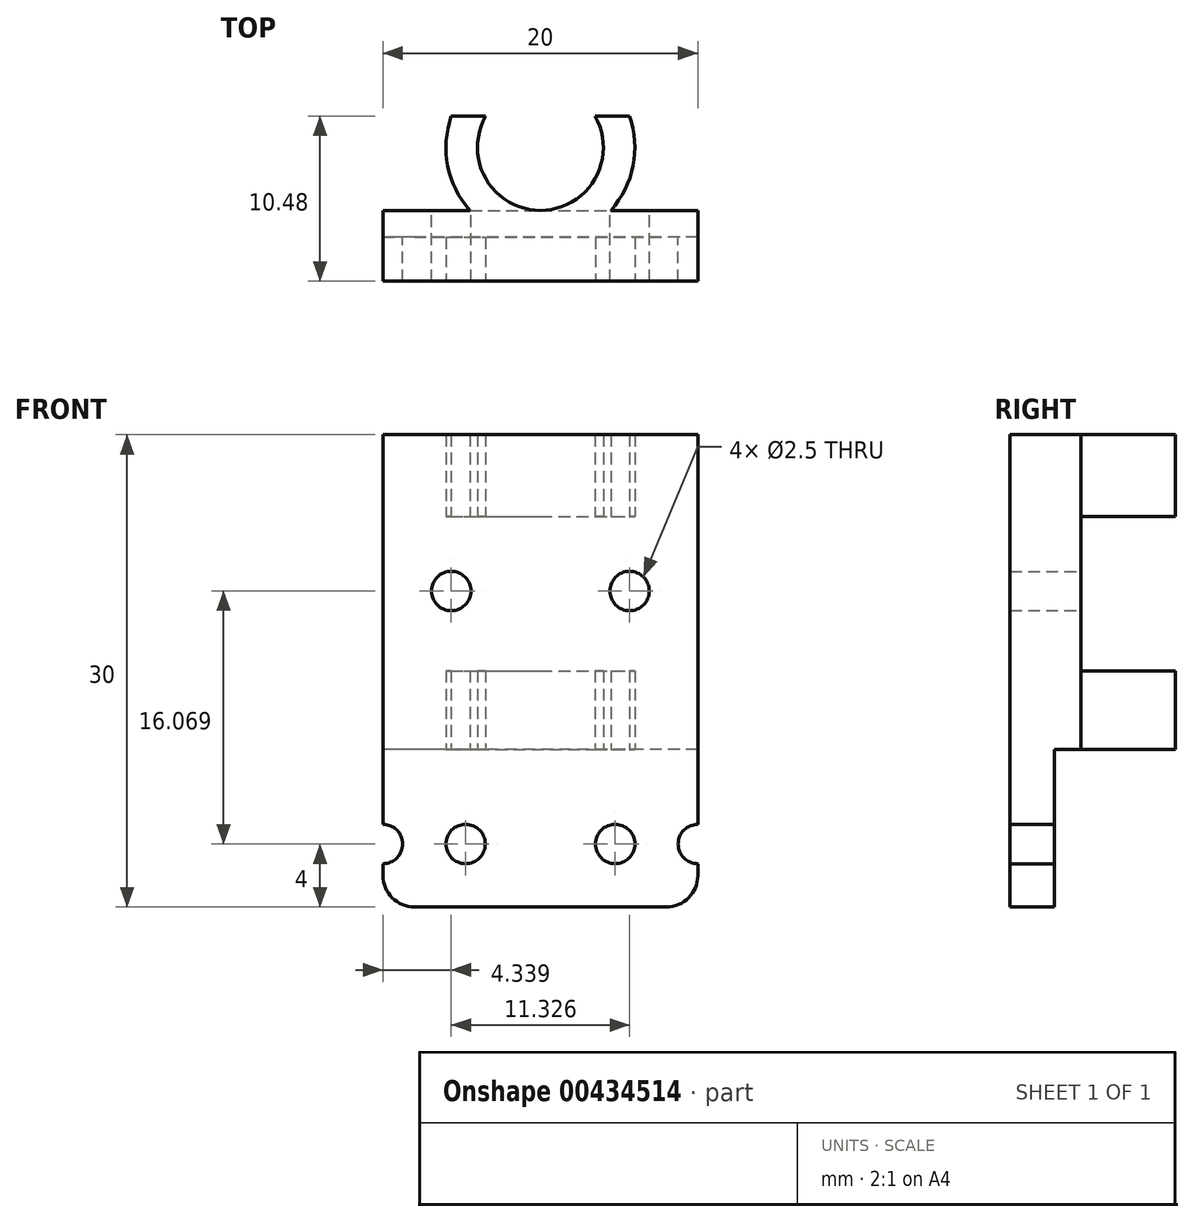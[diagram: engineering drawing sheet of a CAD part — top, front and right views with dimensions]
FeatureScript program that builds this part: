
annotation { "Feature Type Name" : "Feature", "Feature Type Description" : "" }
export const myFeature = defineFeature(function(context is Context, id is Id, definition is map)
    precondition{}
    {
        {
            var Q0;
            Q0=qCreatedBy(makeId("Top.planeOp"),FACE);
            var sketch = newSketch(context, id + "F0", { "sketchPlane" : qUnion([Q0])});
            skArc(sketch, "E0", {"start": v(-19.61, 7.8) * mm, "mid": v(-13.95, -0.17) * mm, "end": v(-8.28, 7.8) * mm});
            skLineSegment(sketch, "E1.right", {"start": v(278.54, 89.36) * mm, "end": v(278.54, 0) * mm});
            skArc(sketch, "E2", {"start": v(-17.42, 7.8) * mm, "mid": v(-13.95, 1.83) * mm, "end": v(-10.47, 7.8) * mm});
            skLineSegment(sketch, "E3.top", {"start": v(-19.61, 7.8) * mm, "end": v(-17.42, 7.8) * mm});
            skLineSegment(sketch, "E4.trimOffspring", {"start": v(-10.47, 7.8) * mm, "end": v(-8.28, 7.8) * mm});
            skPoint(sketch, "E5", {"position": v(-13.95, -1.45) * mm});
            skLineSegment(sketch, "E6", {"start": v(-13.95, 7.55) * mm, "end": v(-13.95, -10.44) * mm, "construction": true});
            skPoint(sketch, "E7.startSnap0", {"position": v(-13.95, 1.83) * mm});
            skSolve(sketch);
        }
        {
            var Q0;
            Q0=qSketchRegion(id+"F0",true);
            extrude(context, id + "F1", {"entities" : qUnion([Q0]), "depth" : 20 * mm});
        }
        {
            var Q0;
            Q0=qCreatedBy(makeId("Top.planeOp"),FACE);
            var sketch = newSketch(context, id + "F2", { "sketchPlane" : qUnion([Q0])});
            skArc(sketch, "E8.0.0", {"start": v(-17.42, 7.8) * mm, "mid": v(-13.95, 1.83) * mm, "end": v(-10.47, 7.8) * mm, "construction": true});
            skLineSegment(sketch, "E8.0.1", {"start": v(-10.47, 7.8) * mm, "end": v(-8.28, 7.8) * mm, "construction": true});
            skArc(sketch, "E8.0.2", {"start": v(-8.28, 7.8) * mm, "mid": v(-13.95, -0.17) * mm, "end": v(-19.61, 7.8) * mm, "construction": true});
            skLineSegment(sketch, "E8.0.3", {"start": v(-19.61, 7.8) * mm, "end": v(-17.42, 7.8) * mm, "construction": true});
            skPoint(sketch, "E9", {"position": v(-13.95, -0.17) * mm});
            skPoint(sketch, "E10", {"position": v(-13.95, 1.83) * mm});
            skLineSegment(sketch, "E11", {"start": v(-13.95, 1.83) * mm, "end": v(-3.95, 1.83) * mm});
            skLineSegment(sketch, "E12", {"start": v(-3.95, 1.83) * mm, "end": v(-3.95, -1.17) * mm});
            skLineSegment(sketch, "E13", {"start": v(-3.95, -1.17) * mm, "end": v(-23.95, -1.17) * mm});
            skLineSegment(sketch, "E14", {"start": v(-23.95, -1.17) * mm, "end": v(-23.95, 1.83) * mm});
            skLineSegment(sketch, "E15", {"start": v(-23.95, 1.83) * mm, "end": v(-13.95, 1.83) * mm});
            skSolve(sketch);
        }
        {
            var Q0;
            Q0=makeQuery(id+"F2.imprint","IMPRINT",FACE,{"disambiguationData":[TD([[makeQuery(id+"F2.imprint","IMPRINT",EDGE,{"derivedFrom":sQuery(id+"F2.wireOp",EDGE,"E11")}),-1.0]])]});
            extrude(context, id + "F3", {"entities" : qUnion([Q0]), "operationType" : NewBodyOperationType.ADD, "endBound" : BoundingType.SYMMETRIC, "depth" : 20 * mm});
        }
        {
            var Q0;
            Q0=qCreatedBy(makeId("Front.planeOp"),FACE);
            var sketch = newSketch(context, id + "F4", { "sketchPlane" : qUnion([Q0])});
            skCircle(sketch, "E16", {"center": v(-9.2, -6) * mm, "radius": 1.25 * mm});
            skPoint(sketch, "E17", {"position": v(-10.9, 30) * mm});
            skPoint(sketch, "E18.endSnap0", {"position": v(-14.04, 0) * mm});
            skLineSegment(sketch, "E19.0", {"start": v(-23.95, -10) * mm, "end": v(-3.95, -10) * mm, "construction": true});
            skPoint(sketch, "E20", {"position": v(-13.95, -10) * mm});
            skLineSegment(sketch, "E21", {"start": v(-13.95, -10) * mm, "end": v(-13.95, -0.98) * mm, "construction": true});
            skCircle(sketch, "E22.MirrorC", {"center": v(-18.7, -6) * mm, "radius": 1.25 * mm});
            skSolve(sketch);
        }
        {
            var Q0;
            Q0 = qSketchRegion(id + "F4", true);
            extrude(context, id + "F5", {"entities" : qUnion([Q0]), "operationType" : NewBodyOperationType.REMOVE, "endBound" : BoundingType.SYMMETRIC, "oppositeDirection" : true, "depth" : 4.4 * mm});
        }
        {
            var Q0;
            Q0=makeQuery(id+"F3.opExtrude","CAP_FACE",FACE,{"disambiguationData":[OSD([sQuery(id+"F2.wireOp",EDGE,"E11"),sQuery(id+"F2.wireOp",EDGE,"E12"),sQuery(id+"F2.wireOp",EDGE,"E13"),sQuery(id+"F2.wireOp",EDGE,"E14"),sQuery(id+"F2.wireOp",EDGE,"E15")])],"isStart":false});
            var sketch = newSketch(context, id + "F6", { "sketchPlane" : qUnion([Q0])});
            skArc(sketch, "E23.0.0", {"start": v(-9.48, 1.83) * mm, "mid": v(-13.95, -0.17) * mm, "end": v(-18.42, 1.83) * mm});
            skLineSegment(sketch, "E23.0.1", {"start": v(-18.42, 1.83) * mm, "end": v(-23.95, 1.83) * mm});
            skLineSegment(sketch, "E23.0.2", {"start": v(-23.95, 1.83) * mm, "end": v(-23.95, -1.17) * mm});
            skLineSegment(sketch, "E23.0.3", {"start": v(-23.95, -1.17) * mm, "end": v(-3.95, -1.17) * mm});
            skLineSegment(sketch, "E23.0.4", {"start": v(-3.95, -1.17) * mm, "end": v(-3.95, 1.83) * mm});
            skLineSegment(sketch, "E23.0.5", {"start": v(-3.95, 1.83) * mm, "end": v(-9.48, 1.83) * mm});
            skSolve(sketch);
        }
        {
            var Q0;
            Q0 = qSketchRegion(id + "F6", true);
            var Q1;
            Q1=makeQuery(id+"F1.opExtrude","CAP_FACE",FACE,{"disambiguationData":[OSD([sQuery(id+"F0.wireOp",EDGE,"E0"),sQuery(id+"F0.wireOp",EDGE,"E2"),sQuery(id+"F0.wireOp",EDGE,"E3.top"),sQuery(id+"F0.wireOp",EDGE,"E4.trimOffspring")])],"isStart":false});
            extrude(context, id + "F7", {"entities" : qUnion([Q0]), "operationType" : NewBodyOperationType.ADD, "endBound" : BoundingType.UP_TO_SURFACE, "endBoundEntityFace" : qUnion([Q1]), "depth" : 6.4 * mm});
        }
        {
            var Q0;
            Q0=makeQuery(id+"F7.boolean.opBoolean","MERGE",FACE,{"derivedFrom":[makeQuery(id+"F3.opExtrude","SWEPT_FACE",FACE,{"disambiguationData":[OSD([sQuery(id+"F2.wireOp",EDGE,"E11"),sQuery(id+"F2.wireOp",EDGE,"E15")])]}),makeQuery(id+"F7.opExtrude","SWEPT_FACE",FACE,{"disambiguationData":[OSD([sQuery(id+"F6.wireOp",EDGE,"E23.0.1")])]}),makeQuery(id+"F7.opExtrude","SWEPT_FACE",FACE,{"disambiguationData":[OSD([sQuery(id+"F6.wireOp",EDGE,"E23.0.5")])]})]});
            cPlane(context, id + "F8", {"entities" : qUnion([Q0]), "cplaneType" : CPlaneType.OFFSET, "offset" : 25 * mm, "width" : 150 * mm, "height" : 150 * mm});
        }
        {
            var Q0;
            Q0=qCreatedBy(id+"F8.planeOp",FACE);
            var sketch = newSketch(context, id + "F9", { "sketchPlane" : qUnion([Q0])});
            skPoint(sketch, "E24.0", {"position": v(18.7, -6) * mm});
            skPoint(sketch, "E25.0", {"position": v(9.2, -6) * mm});
            skLineSegment(sketch, "E26", {"start": v(1.82, -6) * mm, "end": v(28.97, -6) * mm, "construction": true});
            skLineSegment(sketch, "E27.0", {"start": v(3.95, 20) * mm, "end": v(3.95, -10) * mm, "construction": true});
            skLineSegment(sketch, "E28.0", {"start": v(23.95, 20) * mm, "end": v(23.95, -10) * mm, "construction": true});
            skPoint(sketch, "E29", {"position": v(3.95, -6) * mm});
            skPoint(sketch, "E30", {"position": v(23.95, -6) * mm});
            skCircle(sketch, "E31.0", {"center": v(9.2, -6) * mm, "radius": 1.25 * mm, "construction": true});
            skCircle(sketch, "E32", {"center": v(23.95, -6) * mm, "radius": 1.25 * mm});
            skCircle(sketch, "E33.MirrorC", {"center": v(3.95, -6) * mm, "radius": 1.25 * mm});
            skSolve(sketch);
        }
        {
            var Q0;
            Q0 = qSketchRegion(id + "F9", true);
            extrude(context, id + "F10", {"entities" : qUnion([Q0]), "operationType" : NewBodyOperationType.REMOVE, "endBound" : BoundingType.THROUGH_ALL, "oppositeDirection" : true, "depth" : 25 * mm});
        }
        {
            var Q0;
            Q0=makeQuery(id+"F3.opExtrude","CAP_EDGE",EDGE,{"disambiguationData":[OSD([sQuery(id+"F2.wireOp",EDGE,"E14")])],"isStart":true});
            var Q1;
            Q1=makeQuery(id+"F3.opExtrude","CAP_EDGE",EDGE,{"disambiguationData":[OSD([sQuery(id+"F2.wireOp",EDGE,"E12")])],"isStart":true});
            fillet(context, id + "F11", {"entities" : qUnion([Q0, Q1]), "radius" : 2 * mm, "tangentPropagation" : true, "allowEdgeOverflow" : false});
        }
        {
            var Q0;
            Q0=makeQuery(id+"F7.boolean.opBoolean","MERGE",FACE,{"derivedFrom":[makeQuery(id+"F3.opExtrude","SWEPT_FACE",FACE,{"disambiguationData":[OSD([sQuery(id+"F2.wireOp",EDGE,"E13")])]}),makeQuery(id+"F7.opExtrude","SWEPT_FACE",FACE,{"disambiguationData":[OSD([sQuery(id+"F6.wireOp",EDGE,"E23.0.3")])]})]});
            cPlane(context, id + "F12", {"entities" : qUnion([Q0]), "cplaneType" : CPlaneType.OFFSET, "offset" : 0 * mm, "width" : 150 * mm, "height" : 150 * mm});
        }
        {
            var Q0;
            Q0=qCreatedBy(id+"F12.planeOp",FACE);
            var sketch = newSketch(context, id + "F13", { "sketchPlane" : qUnion([Q0])});
            skLineSegment(sketch, "E34.0.0", {"start": v(-23.95, -7.25) * mm, "end": v(-23.95, -8) * mm});
            skArc(sketch, "E34.0.1", {"start": v(-23.95, -8) * mm, "mid": v(-23.36, -9.41) * mm, "end": v(-21.95, -10) * mm});
            skLineSegment(sketch, "E34.0.2", {"start": v(-21.95, -10) * mm, "end": v(-5.95, -10) * mm});
            skArc(sketch, "E34.0.3", {"start": v(-5.95, -10) * mm, "mid": v(-4.53, -9.41) * mm, "end": v(-3.95, -8) * mm});
            skLineSegment(sketch, "E34.0.4", {"start": v(-3.95, -8) * mm, "end": v(-3.95, -7.25) * mm});
            skArc(sketch, "E34.0.5", {"start": v(-3.95, -7.25) * mm, "mid": v(-5.2, -6) * mm, "end": v(-3.95, -4.75) * mm});
            skLineSegment(sketch, "E34.0.6", {"start": v(-3.95, -4.75) * mm, "end": v(-3.95, 20) * mm});
            skLineSegment(sketch, "E34.0.7", {"start": v(-3.95, 20) * mm, "end": v(-23.95, 20) * mm});
            skLineSegment(sketch, "E34.0.8", {"start": v(-23.95, 20) * mm, "end": v(-23.95, -4.75) * mm});
            skArc(sketch, "E34.0.9", {"start": v(-23.95, -4.75) * mm, "mid": v(-22.7, -6) * mm, "end": v(-23.95, -7.25) * mm});
            skSolve(sketch);
        }
        {
            var Q0;
            Q0 = qSketchRegion(id + "F13", true);
            extrude(context, id + "F14", {"entities" : qUnion([Q0]), "operationType" : NewBodyOperationType.ADD, "depth" : 1.5 * mm});
        }
        {
            var Q0;
            Q0=makeQuery(id+"F7.boolean.opBoolean","MERGE",FACE,{"derivedFrom":[makeQuery(id+"F3.opExtrude","SWEPT_FACE",FACE,{"disambiguationData":[OSD([sQuery(id+"F2.wireOp",EDGE,"E11"),sQuery(id+"F2.wireOp",EDGE,"E15")])]}),makeQuery(id+"F7.opExtrude","SWEPT_FACE",FACE,{"disambiguationData":[OSD([sQuery(id+"F6.wireOp",EDGE,"E23.0.1")])]}),makeQuery(id+"F7.opExtrude","SWEPT_FACE",FACE,{"disambiguationData":[OSD([sQuery(id+"F6.wireOp",EDGE,"E23.0.5")])]})]});
            cPlane(context, id + "F15", {"entities" : qUnion([Q0]), "cplaneType" : CPlaneType.OFFSET, "offset" : 0 * mm, "width" : 150 * mm, "height" : 150 * mm});
        }
        {
            var Q0;
            Q0=qCreatedBy(id+"F8.planeOp",FACE);
            var sketch = newSketch(context, id + "F16", { "sketchPlane" : qUnion([Q0])});
            skPoint(sketch, "E35.0", {"position": v(3.95, 0) * mm});
            skPoint(sketch, "E36.0", {"position": v(23.95, 0) * mm});
            skPoint(sketch, "E37.0", {"position": v(23.95, -10) * mm});
            skPoint(sketch, "E38.0", {"position": v(3.95, -10) * mm});
            skLineSegment(sketch, "E39", {"start": v(3.95, 0) * mm, "end": v(23.95, 0) * mm});
            skLineSegment(sketch, "E40", {"start": v(23.95, 0) * mm, "end": v(23.95, -10) * mm});
            skLineSegment(sketch, "E41", {"start": v(23.95, -10) * mm, "end": v(3.95, -10) * mm});
            skLineSegment(sketch, "E42", {"start": v(3.95, -10) * mm, "end": v(3.95, 0) * mm});
            skSolve(sketch);
        }
        {
            var Q0;
            Q0 = qSketchRegion(id + "F16", true);
            extrude(context, id + "F17", {"entities" : qUnion([Q0]), "operationType" : NewBodyOperationType.REMOVE, "oppositeDirection" : true, "depth" : 26.7 * mm});
        }
        {
            var Q0;
            Q0=qCreatedBy(makeId("Front.planeOp"),FACE);
            cPlane(context, id + "F18", {"entities" : qUnion([Q0]), "cplaneType" : CPlaneType.OFFSET, "offset" : 25 * mm, "width" : 150 * mm, "height" : 150 * mm});
        }
        {
            var Q0;
            Q0=qCreatedBy(id+"F18.planeOp",FACE);
            var sketch = newSketch(context, id + "F19", { "sketchPlane" : qUnion([Q0])});
            skCircle(sketch, "E43.0", {"center": v(-9.2, -6) * mm, "radius": 1.25 * mm});
            skCircle(sketch, "E44.0", {"center": v(-18.7, -6) * mm, "radius": 1.25 * mm});
            skSolve(sketch);
        }
        {
            var Q0;
            Q0 = qSketchRegion(id + "F19", true);
            extrude(context, id + "F20", {"entities" : qUnion([Q0]), "operationType" : NewBodyOperationType.REMOVE, "oppositeDirection" : true, "depth" : 32.1 * mm});
        }
        {
            var Q0;
            Q0=qCreatedBy(makeId("Top.planeOp"),FACE);
            cPlane(context, id + "F21", {"entities" : qUnion([Q0]), "cplaneType" : CPlaneType.OFFSET, "offset" : 11.9 * mm, "width" : 150 * mm, "height" : 150 * mm});
        }
        {
            var Q0;
            Q0=qCreatedBy(id+"F21.planeOp",FACE);
            var sketch = newSketch(context, id + "F22", { "sketchPlane" : qUnion([Q0])});
            skArc(sketch, "E45.0.0", {"start": v(-10.47, 7.8) * mm, "mid": v(-13.95, 1.83) * mm, "end": v(-17.42, 7.8) * mm, "construction": true});
            skLineSegment(sketch, "E45.0.1", {"start": v(-17.42, 7.8) * mm, "end": v(-19.61, 7.8) * mm, "construction": true});
            skArc(sketch, "E45.0.2", {"start": v(-19.61, 7.8) * mm, "mid": v(-19.83, 4.65) * mm, "end": v(-18.42, 1.83) * mm, "construction": true});
            skLineSegment(sketch, "E45.0.3", {"start": v(-18.42, 1.83) * mm, "end": v(-23.95, 1.83) * mm, "construction": true});
            skLineSegment(sketch, "E45.0.4", {"start": v(-23.95, 1.83) * mm, "end": v(-23.95, -2.67) * mm, "construction": true});
            skLineSegment(sketch, "E45.0.5", {"start": v(-23.95, -2.67) * mm, "end": v(-3.95, -2.67) * mm, "construction": true});
            skLineSegment(sketch, "E45.0.6", {"start": v(-3.95, -2.67) * mm, "end": v(-3.95, 1.83) * mm, "construction": true});
            skLineSegment(sketch, "E45.0.7", {"start": v(-3.95, 1.83) * mm, "end": v(-9.48, 1.83) * mm, "construction": true});
            skArc(sketch, "E45.0.8", {"start": v(-9.48, 1.83) * mm, "mid": v(-8.06, 4.65) * mm, "end": v(-8.28, 7.8) * mm, "construction": true});
            skLineSegment(sketch, "E45.0.9", {"start": v(-8.28, 7.8) * mm, "end": v(-10.47, 7.8) * mm, "construction": true});
            skLineSegment(sketch, "E46.bottom", {"start": v(-23.95, 1.83) * mm, "end": v(-3.95, 1.83) * mm});
            skLineSegment(sketch, "E46.top", {"start": v(-23.95, 11.1) * mm, "end": v(-3.95, 11.1) * mm});
            skLineSegment(sketch, "E46.left", {"start": v(-23.95, 1.83) * mm, "end": v(-23.95, 11.1) * mm});
            skLineSegment(sketch, "E46.right", {"start": v(-3.95, 1.83) * mm, "end": v(-3.95, 11.1) * mm});
            skSolve(sketch);
        }
        {
            var Q0;
            Q0 = qSketchRegion(id + "F22", true);
            extrude(context, id + "F23", {"entities" : qUnion([Q0]), "operationType" : NewBodyOperationType.REMOVE, "oppositeDirection" : true, "depth" : 6.9 * mm});
        }
        {
            var Q0;
            Q0 = qSketchRegion(id + "F22", true);
            extrude(context, id + "F24", {"entities" : qUnion([Q0]), "operationType" : NewBodyOperationType.REMOVE, "depth" : 2.9 * mm});
        }
        {
            var Q0;
            Q0=qCreatedBy(id+"F15.planeOp",FACE);
            var sketch = newSketch(context, id + "F25", { "sketchPlane" : qUnion([Q0])});
            skLineSegment(sketch, "E47.0", {"start": v(23.95, 11.9) * mm, "end": v(3.95, 11.9) * mm, "construction": true});
            skPoint(sketch, "E48.0", {"position": v(8.28, 11.9) * mm});
            skLineSegment(sketch, "E49", {"start": v(8.28, 14.8) * mm, "end": v(8.28, 5.33) * mm, "construction": true});
            skLineSegment(sketch, "E50", {"start": v(13.95, 14.95) * mm, "end": v(13.95, 5.19) * mm, "construction": true});
            skPoint(sketch, "E50.startSnap0", {"position": v(13.95, 11.9) * mm});
            skCircle(sketch, "E51", {"center": v(8.28, 10.07) * mm, "radius": 1.25 * mm});
            skCircle(sketch, "E52.MirrorC", {"center": v(19.61, 10.07) * mm, "radius": 1.25 * mm});
            skSolve(sketch);
        }
        {
            var Q0;
            Q0 = qSketchRegion(id + "F25", true);
            extrude(context, id + "F26", {"entities" : qUnion([Q0]), "operationType" : NewBodyOperationType.REMOVE, "endBound" : BoundingType.SYMMETRIC, "oppositeDirection" : true, "depth" : 25 * mm});
        }
    });
